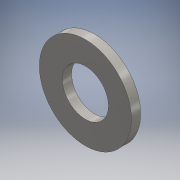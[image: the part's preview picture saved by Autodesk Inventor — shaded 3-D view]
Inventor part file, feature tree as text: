
AUTODESK INVENTOR PART (.ipt)
format: ipt  version: 2016 (Build 200138000, 138)  size: 109,568 bytes
history: native  units: mm
features: extrude x1, sketch x1
ambient origin geometry x8: Origin, YZ Plane, XZ Plane, XY Plane, X Axis, Y Axis, Z Axis, Center Point
bodies: Solid1 (feature_tree)
feature tree (2):
  extrude  "Extrusion1"  Depth=10.0mm
  sketch  "Sketch1"  dims[d0=5.0mm d1=10.0mm d2=1.0mm d3=0.0mm]
